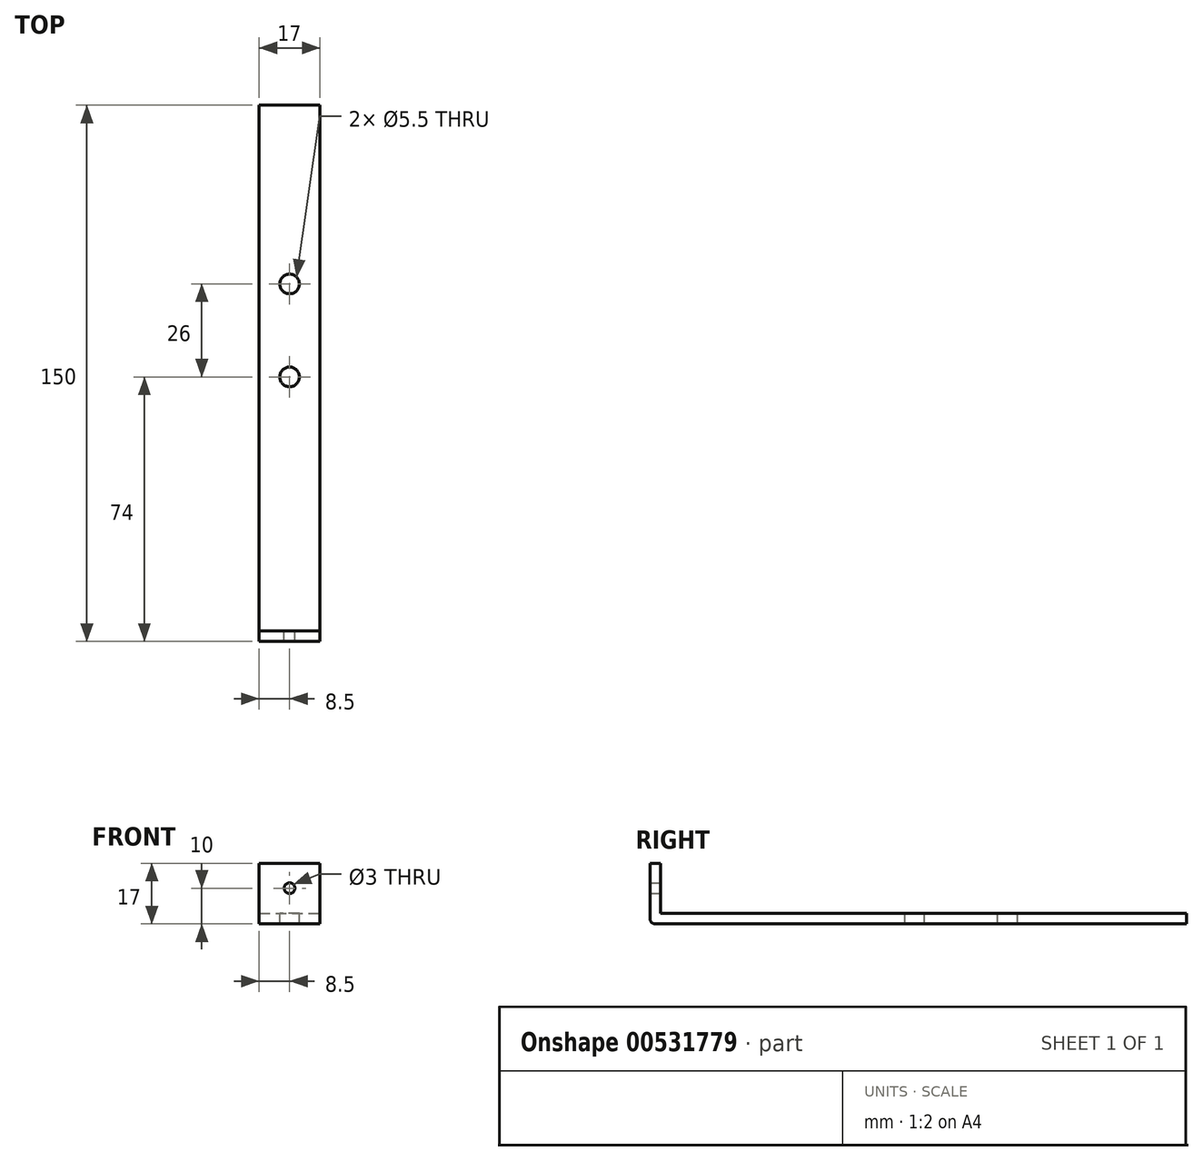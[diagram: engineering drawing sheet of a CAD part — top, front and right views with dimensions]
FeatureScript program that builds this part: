
annotation { "Feature Type Name" : "Feature", "Feature Type Description" : "" }
export const myFeature = defineFeature(function(context is Context, id is Id, definition is map)
    precondition{}
    {
        {
            var Q0;
            Q0=qCreatedBy(makeId("Top.planeOp"),FACE);
            var sketch = newSketch(context, id + "F0", { "sketchPlane" : qUnion([Q0])});
            skLineSegment(sketch, "E0.bottom", {"start": v(-8.5, -75) * mm, "end": v(8.5, -75) * mm});
            skLineSegment(sketch, "E0.top", {"start": v(-8.5, 75) * mm, "end": v(8.5, 75) * mm});
            skLineSegment(sketch, "E0.left", {"start": v(-8.5, -75) * mm, "end": v(-8.5, 75) * mm});
            skLineSegment(sketch, "E0.right", {"start": v(8.5, -75) * mm, "end": v(8.5, 75) * mm});
            skPoint(sketch, "E0.middle", {"position": v(0, 0) * mm});
            skLineSegment(sketch, "E1.bottom", {"start": v(-8.5, -72) * mm, "end": v(8.5, -72) * mm});
            skLineSegment(sketch, "E1.left", {"start": v(-8.5, -72) * mm, "end": v(-8.5, -75) * mm});
            skLineSegment(sketch, "E1.right", {"start": v(8.5, -72) * mm, "end": v(8.5, -75) * mm});
            skSolve(sketch);
        }
        {
            var Q0;
            Q0=makeQuery(id+"F0.imprint","IMPRINT",FACE,{"disambiguationData":[TD([[makeQuery(id+"F0.imprint","IMPRINT",EDGE,{"derivedFrom":sQuery(id+"F0.wireOp",EDGE,"E1.bottom")}),-1.0]])]});
            extrude(context, id + "F1", {"entities" : qUnion([Q0]), "depth" : 14 * mm, "offsetDistance" : 25 * mm});
        }
        {
            var Q0;
            Q0=makeQuery(id+"F0.imprint","IMPRINT",FACE,{"disambiguationData":[TD([[makeQuery(id+"F0.imprint","IMPRINT",EDGE,{"derivedFrom":sQuery(id+"F0.wireOp",EDGE,"E0.top")}),-1.0]])]});
            var Q1;
            Q1=makeQuery(id+"F1.opExtrude","CAP_FACE",FACE,{"disambiguationData":[OSD([sQuery(id+"F0.wireOp",EDGE,"E1.bottom"),sQuery(id+"F0.wireOp",EDGE,"E0.bottom"),sQuery(id+"F0.wireOp",EDGE,"E1.left"),sQuery(id+"F0.wireOp",EDGE,"E1.right")])],"isStart":true});
            extrude(context, id + "F2", {"entities" : qUnion([Q0, Q1]), "operationType" : NewBodyOperationType.ADD, "oppositeDirection" : true, "depth" : 3 * mm, "offsetDistance" : 25 * mm});
        }
        {
            var Q0;
            Q0=makeQuery(id+"F1.opExtrude","SWEPT_FACE",FACE,{"disambiguationData":[OSD([sQuery(id+"F0.wireOp",EDGE,"E1.bottom")])]});
            var sketch = newSketch(context, id + "F3", { "sketchPlane" : qUnion([Q0])});
            skCircle(sketch, "E2", {"center": v(0, 7) * mm, "radius": 1.5 * mm});
            skSolve(sketch);
        }
        {
            var Q0;
            Q0=makeQuery(id+"F3.imprint","IMPRINT",FACE,{"disambiguationData":[TD([[makeQuery(id+"F3.imprint","IMPRINT",EDGE,{"derivedFrom":sQuery(id+"F3.wireOp",EDGE,"E2")}),1.0]])]});
            extrude(context, id + "F4", {"entities" : qUnion([Q0]), "operationType" : NewBodyOperationType.REMOVE, "oppositeDirection" : true, "depth" : 25 * mm, "offsetDistance" : 25 * mm});
        }
        {
            var Q0;
            {var subQ0=sQuery(id+"F0.wireOp",EDGE,"E1.bottom");Q0=makeQuery(id+"F2.boolean.opBoolean","MERGE",FACE,{"derivedFrom":[makeQuery(id+"F2.opExtrude","CAP_FACE",FACE,{"disambiguationData":[OSD([sQuery(id+"F0.wireOp",EDGE,"E0.top"),sQuery(id+"F0.wireOp",EDGE,"E0.left"),sQuery(id+"F0.wireOp",EDGE,"E0.right"),subQ0])],"isStart":true}),makeQuery(id+"F2.opExtrude","CAP_FACE",FACE,{"disambiguationData":[OSD([subQ0,sQuery(id+"F0.wireOp",EDGE,"E0.bottom"),sQuery(id+"F0.wireOp",EDGE,"E1.left"),sQuery(id+"F0.wireOp",EDGE,"E1.right")])],"isStart":true})]});}
            var sketch = newSketch(context, id + "F5", { "sketchPlane" : qUnion([Q0])});
            skCircle(sketch, "E3", {"center": v(0, -1) * mm, "radius": 2.75 * mm});
            skCircle(sketch, "E4", {"center": v(0, 25) * mm, "radius": 2.75 * mm});
            skSolve(sketch);
        }
        {
            var Q0;
            Q0=makeQuery(id+"F5.imprint","IMPRINT",FACE,{"disambiguationData":[TD([[makeQuery(id+"F5.imprint","IMPRINT",EDGE,{"derivedFrom":sQuery(id+"F5.wireOp",EDGE,"E3")}),1.0]])]});
            var Q1;
            Q1=makeQuery(id+"F5.imprint","IMPRINT",FACE,{"disambiguationData":[TD([[makeQuery(id+"F5.imprint","IMPRINT",EDGE,{"derivedFrom":sQuery(id+"F5.wireOp",EDGE,"E4")}),1.0]])]});
            extrude(context, id + "F6", {"entities" : qUnion([Q0, Q1]), "operationType" : NewBodyOperationType.REMOVE, "oppositeDirection" : true, "depth" : 25 * mm, "offsetDistance" : 25 * mm});
        }
        {
            var Q0;
            Q0=makeQuery(id+"F2.opExtrude","CAP_EDGE",EDGE,{"disambiguationData":[OSD([sQuery(id+"F0.wireOp",EDGE,"E0.bottom")])],"isStart":false});
            var Q1;
            Q1=makeQuery(id+"F1.opExtrude","CAP_EDGE",EDGE,{"disambiguationData":[OSD([sQuery(id+"F0.wireOp",EDGE,"E1.bottom")])],"isStart":true});
            fillet(context, id + "F7", {"entities" : qUnion([Q0, Q1]), "radius" : 1.5 * mm, "tangentPropagation" : true, "allowEdgeOverflow" : false});
        }
    });
